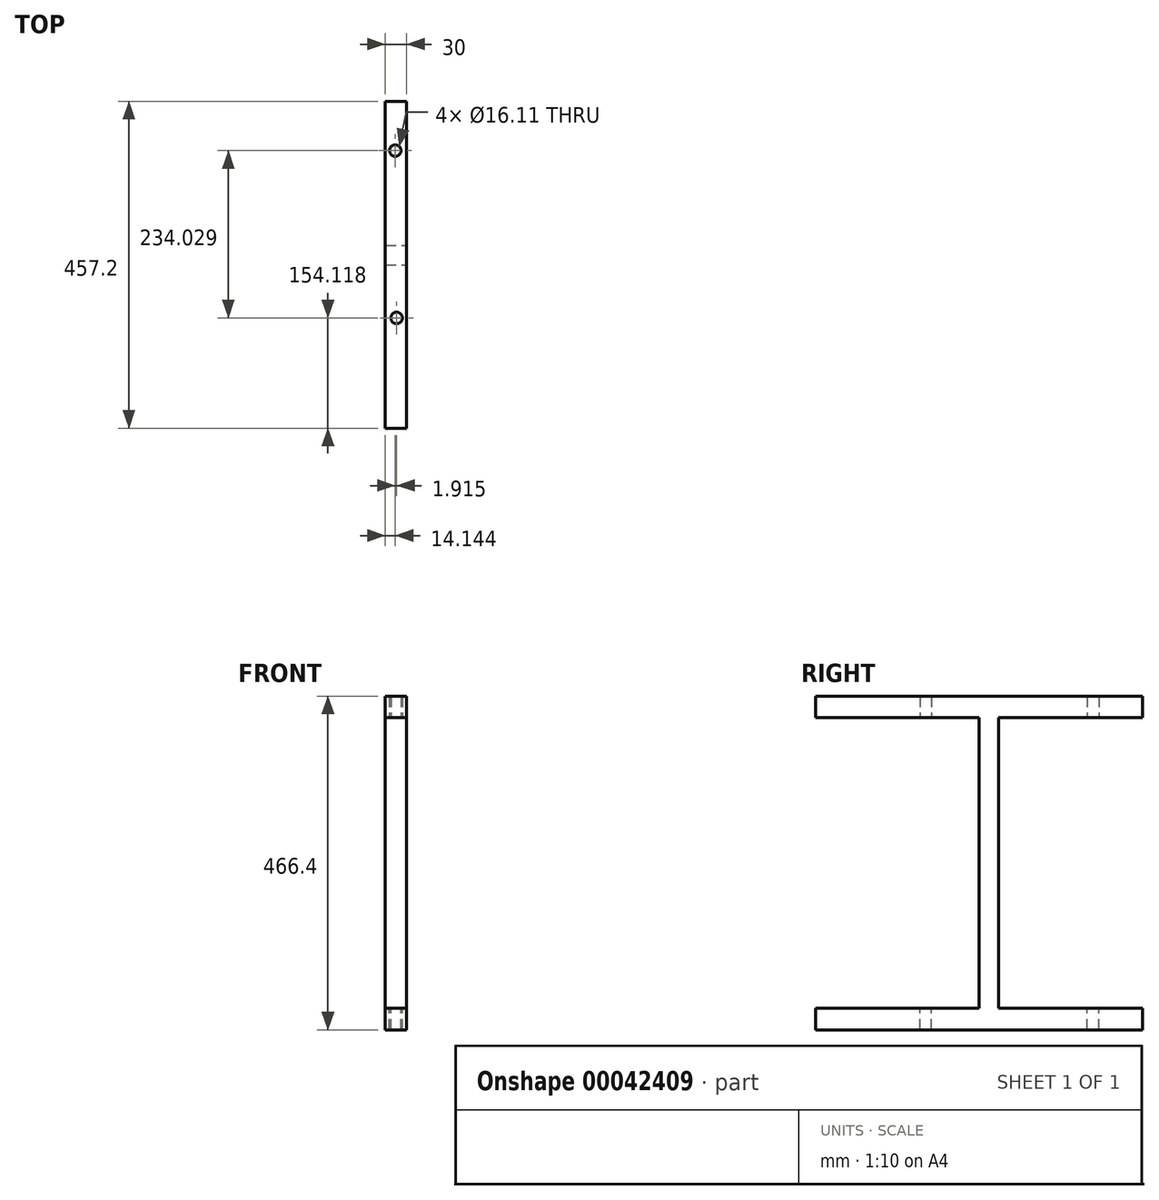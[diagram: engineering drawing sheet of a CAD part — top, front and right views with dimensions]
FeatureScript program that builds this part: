
annotation { "Feature Type Name" : "Feature", "Feature Type Description" : "" }
export const myFeature = defineFeature(function(context is Context, id is Id, definition is map)
    precondition{}
    {
        {
            var Q0;
            Q0=qCreatedBy(makeId("Front.planeOp"),FACE);
            var sketch = newSketch(context, id + "F0", { "sketchPlane" : qUnion([Q0])});
            skLineSegment(sketch, "E0.bottom", {"start": v(0, 0) * mm, "end": v(30, 0) * mm});
            skLineSegment(sketch, "E0.top", {"start": v(0, 30) * mm, "end": v(30, 30) * mm});
            skLineSegment(sketch, "E0.left", {"start": v(0, 0) * mm, "end": v(0, 30) * mm});
            skLineSegment(sketch, "E0.right", {"start": v(30, 0) * mm, "end": v(30, 30) * mm});
            skSolve(sketch);
        }
        {
            var Q0;
            Q0=makeQuery(id+"F0.imprint","IMPRINT",FACE,{"disambiguationData":[TD([[makeQuery(id+"F0.imprint","IMPRINT",EDGE,{"derivedFrom":sQuery(id+"F0.wireOp",EDGE,"E0.bottom")}),1.0]])]});
            extrude(context, id + "F1", {"entities" : qUnion([Q0]), "depth" : 457.2 * mm});
        }
        {
            var Q0;
            Q0=makeQuery(id+"F1.opExtrude","SWEPT_FACE",FACE,{"disambiguationData":[OSD([sQuery(id+"F0.wireOp",EDGE,"E0.top")])]});
            var sketch = newSketch(context, id + "F2", { "sketchPlane" : qUnion([Q0])});
            skCircle(sketch, "E1", {"center": v(16.06, -303.08) * mm, "radius": 8.05 * mm});
            skCircle(sketch, "E2", {"center": v(14.14, -69.05) * mm, "radius": 8.05 * mm});
            skSolve(sketch);
        }
        {
            var Q0;
            Q0 = qSketchRegion(id + "F2", true);
            extrude(context, id + "F3", {"entities" : qUnion([Q0]), "operationType" : NewBodyOperationType.REMOVE, "endBound" : BoundingType.THROUGH_ALL, "oppositeDirection" : true, "depth" : 25.4 * mm});
        }
        {
            var Q0;
            Q0=makeQuery(id+"F1.opExtrude","SWEPT_FACE",FACE,{"disambiguationData":[OSD([sQuery(id+"F0.wireOp",EDGE,"E0.top")])]});
            cPlane(context, id + "F4", {"entities" : qUnion([Q0]), "cplaneType" : CPlaneType.OFFSET, "offset" : 203.2 * mm, "width" : 152.4 * mm, "height" : 152.4 * mm});
        }
        {
            var Q0;
            Q0=makeQuery(id+"F1.opExtrude","SWEPT_FACE",FACE,{"disambiguationData":[OSD([sQuery(id+"F0.wireOp",EDGE,"E0.top")])]});
            var sketch = newSketch(context, id + "F5", { "sketchPlane" : qUnion([Q0])});
            skLineSegment(sketch, "E3.bottom", {"start": v(0, -228.6) * mm, "end": v(30, -228.6) * mm});
            skLineSegment(sketch, "E3.top", {"start": v(0, -201.28) * mm, "end": v(30, -201.28) * mm});
            skLineSegment(sketch, "E3.left", {"start": v(0, -228.6) * mm, "end": v(0, -201.28) * mm});
            skLineSegment(sketch, "E3.right", {"start": v(30, -228.6) * mm, "end": v(30, -201.28) * mm});
            skSolve(sketch);
        }
        {
            var Q0;
            Q0=makeQuery(id+"F5.imprint","IMPRINT",FACE,{"disambiguationData":[TD([[makeQuery(id+"F5.imprint","IMPRINT",EDGE,{"derivedFrom":sQuery(id+"F5.wireOp",EDGE,"E3.bottom")}),1.0]])]});
            var Q1;
            Q1=sQuery(id+"F5.wireOp",EDGE,"E3.top");
            var Q2;
            Q2=sQuery(id+"F5.wireOp",EDGE,"E3.left");
            extrude(context, id + "F6", {"entities" : qUnion([Q0]), "operationType" : NewBodyOperationType.ADD, "surfaceEntities" : qUnion([Q1, Q2]), "depth" : 203.2 * mm});
        }
        {
            var Q0;
            Q0=makeQuery(id+"F1.opExtrude","SWEPT_BODY",BODY,{"disambiguationData":[OSD([sQuery(id+"F0.wireOp",EDGE,"E0.bottom"),sQuery(id+"F0.wireOp",EDGE,"E0.top"),sQuery(id+"F0.wireOp",EDGE,"E0.left"),sQuery(id+"F0.wireOp",EDGE,"E0.right")])]});
            var Q1;
            Q1=qCreatedBy(id+"F4.planeOp",FACE);
            mirror(context, id + "F7", {"operationType" : NewBodyOperationType.ADD, "entities" : qUnion([Q0]), "mirrorPlane" : qUnion([Q1])});
        }
    });
